# Revit family: NLRS_57_DUF_UN_broekstuk_bocht_bocht_type1_nijburg
name_source: partatom
category: Duct Fittings
units: mm (PartAtom-declared; Revit-internal decimal feet)

## family parameters
Always vertical = Yes
Cut with Voids When Loaded = No
Part Type = Tee
Round Connector Dimension = Use Diameter
Shared = No
Work Plane-Based = No

## types (4) — shared parameters
Assembly Code = 57.70
Description = Rechthoekig broekstuk - 2 radius bochten, verlopend
Manufacturer = Nijburg Industry Group
Model = Broekstuk - bocht+bocht
NLRS_C_content_datum_gewijzigd = 04-05-2023
NLRS_C_content_provider = Nijburg Klimaattechniek
NLRS_C_content_versie = 1.20.00
NLRS_C_description = Rechthoekig broekstuk - 2 radius bochten, verlopend
NLRS_C_model = Broekstuk - bocht+bocht
Type Comments = Links-Rechts
URL = https://nijburg-klimaattechniek.nl
zero-valued in all types: Default Elevation

## type names (no varying parameters)
- R=170-170 (std)
- R=150-150
- R=120-120
- R=100-100

## geometry (parser evidence)
native form markers: Sweep x10
no freeform markers — native parametric forms only
